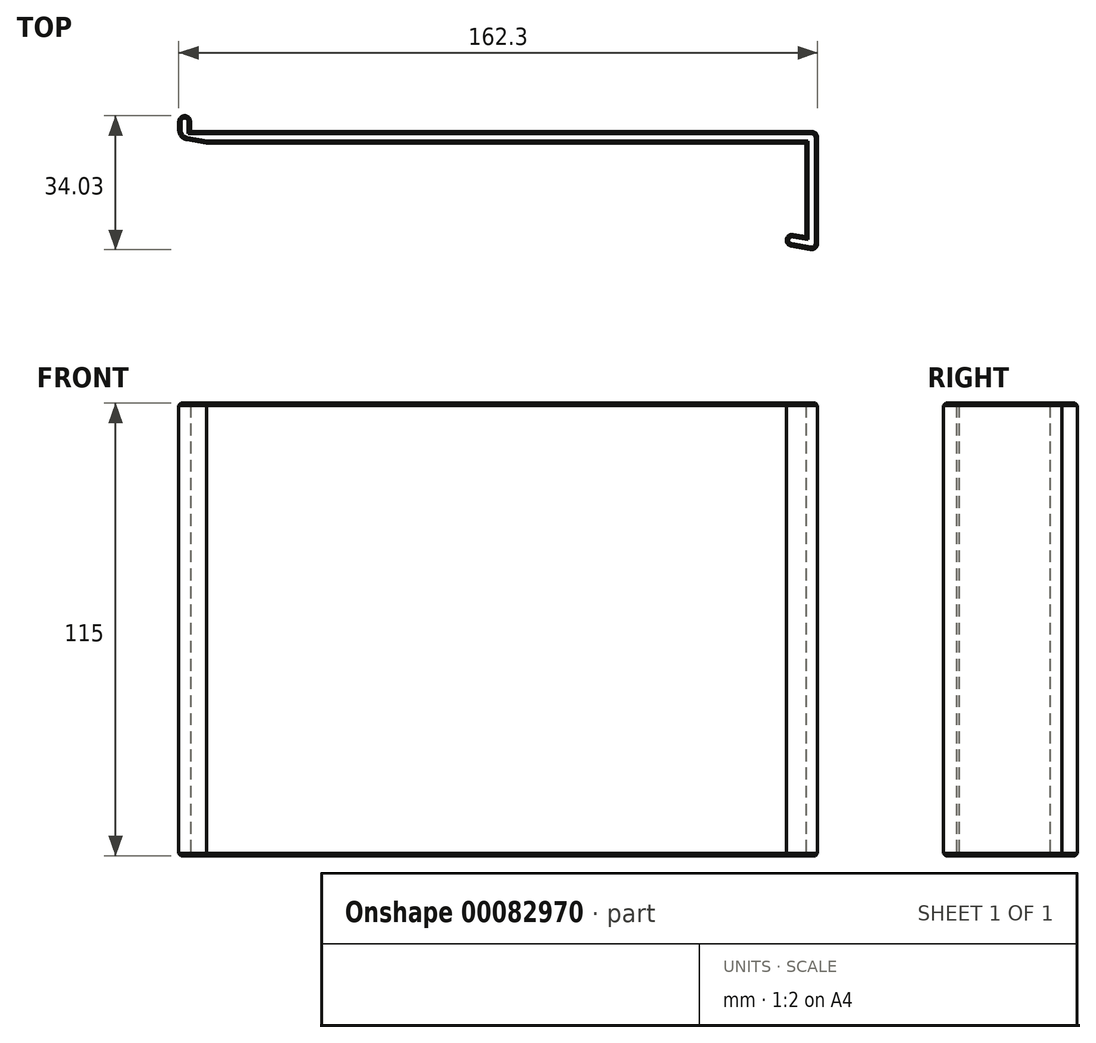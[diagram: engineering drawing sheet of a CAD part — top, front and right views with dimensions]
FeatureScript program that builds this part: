
annotation { "Feature Type Name" : "Feature", "Feature Type Description" : "" }
export const myFeature = defineFeature(function(context is Context, id is Id, definition is map)
    precondition{}
    {
        {
            var Q0;
            Q0=qCreatedBy(makeId("Top.planeOp"),FACE);
            var sketch = newSketch(context, id + "F0", { "sketchPlane" : qUnion([Q0])});
            skLineSegment(sketch, "E0", {"start": v(-73.68, 0.15) * mm, "end": v(87.92, -28.35) * mm, "construction": true});
            skLineSegment(sketch, "E1", {"start": v(-72.86, 0) * mm, "end": v(86.44, 0) * mm, "construction": true});
            skLineSegment(sketch, "E2", {"start": v(86.44, 0) * mm, "end": v(86.44, -27.03) * mm, "construction": true});
            skLineSegment(sketch, "E3", {"start": v(-72.86, 0) * mm, "end": v(-72.86, 4) * mm, "construction": true});
            skArc(sketch, "E4.0.endCap", {"start": v(-74.36, 4) * mm, "mid": v(-72.86, 5.5) * mm, "end": v(-71.36, 4) * mm});
            skLineSegment(sketch, "E4.0.right", {"start": v(-71.36, 1.5) * mm, "end": v(-71.36, 4) * mm});
            skArc(sketch, "E4.1.endCap", {"start": v(86.44, 1.5) * mm, "mid": v(87.5, 1.06) * mm, "end": v(87.94, 0) * mm});
            skLineSegment(sketch, "E4.1.left", {"start": v(-71.36, 1.5) * mm, "end": v(86.44, 1.5) * mm});
            skLineSegment(sketch, "E4.1.right", {"start": v(-67.23, -1.5) * mm, "end": v(84.94, -1.5) * mm});
            skArc(sketch, "E4.2.startCap", {"start": v(86.44, 1.5) * mm, "mid": v(87.5, 1.06) * mm, "end": v(87.94, 0) * mm});
            skLineSegment(sketch, "E4.2.left", {"start": v(87.94, 0) * mm, "end": v(87.94, -27.03) * mm});
            skLineSegment(sketch, "E4.2.right", {"start": v(84.94, -1.5) * mm, "end": v(84.94, -25.29) * mm});
            skLineSegment(sketch, "E5", {"start": v(-74.3, -0.25) * mm, "end": v(98.84, -30.78) * mm, "construction": true});
            skLineSegment(sketch, "E6", {"start": v(-72.3, -0.6) * mm, "end": v(-67.23, -1.5) * mm});
            skLineSegment(sketch, "E7.0.left", {"start": v(-74.36, 1.85) * mm, "end": v(-74.36, 4) * mm});
            skArc(sketch, "E8.filletArc", {"start": v(-74.36, 1.85) * mm, "mid": v(-73.77, 0.25) * mm, "end": v(-72.3, -0.6) * mm});
            skLineSegment(sketch, "E9", {"start": v(86.44, -27.03) * mm, "end": v(81.49, -26.15) * mm, "construction": true});
            skArc(sketch, "E10.0.startCap", {"start": v(86.7, -25.55) * mm, "mid": v(87.6, -26.06) * mm, "end": v(87.94, -27.03) * mm, "construction": true});
            skArc(sketch, "E10.0.endCap", {"start": v(81.23, -27.63) * mm, "mid": v(80.01, -25.9) * mm, "end": v(81.75, -24.68) * mm});
            skLineSegment(sketch, "E10.0.left", {"start": v(86.18, -28.5) * mm, "end": v(81.23, -27.63) * mm});
            skLineSegment(sketch, "E10.0.right", {"start": v(86.7, -25.55) * mm, "end": v(86.44, -25.5) * mm});
            skLineSegment(sketch, "E11", {"start": v(84.94, -25.24) * mm, "end": v(81.75, -24.68) * mm});
            skArc(sketch, "E12", {"start": v(87.94, -27.03) * mm, "mid": v(87.4, -28.18) * mm, "end": v(86.18, -28.5) * mm});
            skLineSegment(sketch, "E13", {"start": v(86.44, -25.5) * mm, "end": v(84.94, -25.24) * mm, "construction": true});
            skSolve(sketch);
        }
        {
            var Q0;
            Q0=makeQuery(id+"F0.imprint","IMPRINT",FACE,{"disambiguationData":[TD([[makeQuery(id+"F0.imprint","IMPRINT",EDGE,{"derivedFrom":sQuery(id+"F0.wireOp",EDGE,"E4.1.left")}),-1.0]])]});
            extrude(context, id + "F1", {"entities" : qUnion([Q0]), "depth" : 115 * mm});
        }
        {
            var Q0;
            Q0=makeQuery(id+"F1.opExtrude","CAP_FACE",FACE,{"disambiguationData":[OSD([sQuery(id+"F0.wireOp",EDGE,"E4.1.left"),sQuery(id+"F0.wireOp",EDGE,"E4.1.right"),sQuery(id+"F0.wireOp",EDGE,"E4.2.startCap"),sQuery(id+"F0.wireOp",EDGE,"E4.2.endCap"),sQuery(id+"F0.wireOp",EDGE,"E4.2.left"),sQuery(id+"F0.wireOp",EDGE,"E4.2.right"),sQuery(id+"F0.wireOp",EDGE,"d1cd1f58-7f58-4357-8960-825e21f9c44b.trimOffspring"),sQuery(id+"F0.wireOp",EDGE,"E6"),sQuery(id+"F0.wireOp",EDGE,"wJUZhSUe-a4mB-g6ER-T7q2-iyXxeMUP8F40"),sQuery(id+"F0.wireOp",EDGE,"E4.0.endCap"),sQuery(id+"F0.wireOp",EDGE,"E7.0.left"),sQuery(id+"F0.wireOp",EDGE,"E4.0.right"),sQuery(id+"F0.wireOp",EDGE,"bff1c694-8324-4202-af59-6a81b360261e.trimOffspring")])],"isStart":false});
            var Q1;
            Q1=makeQuery(id+"F1.opExtrude","CAP_FACE",FACE,{"disambiguationData":[OSD([sQuery(id+"F0.wireOp",EDGE,"E4.1.left"),sQuery(id+"F0.wireOp",EDGE,"E4.1.right"),sQuery(id+"F0.wireOp",EDGE,"E4.2.startCap"),sQuery(id+"F0.wireOp",EDGE,"E4.2.left"),sQuery(id+"F0.wireOp",EDGE,"E4.2.right"),sQuery(id+"F0.wireOp",EDGE,"E6"),sQuery(id+"F0.wireOp",EDGE,"E4.0.endCap"),sQuery(id+"F0.wireOp",EDGE,"E7.0.left"),sQuery(id+"F0.wireOp",EDGE,"E4.0.right"),sQuery(id+"F0.wireOp",EDGE,"E8.filletArc"),sQuery(id+"F0.wireOp",EDGE,"E10.0.endCap"),sQuery(id+"F0.wireOp",EDGE,"E10.0.left"),sQuery(id+"F0.wireOp",EDGE,"E11"),sQuery(id+"F0.wireOp",EDGE,"E12")])],"isStart":true});
            chamfer(context, id + "F2", {"entities" : qUnion([Q0, Q1]), "width" : 0.6 * mm, "tangentPropagation" : true});
        }
    });
